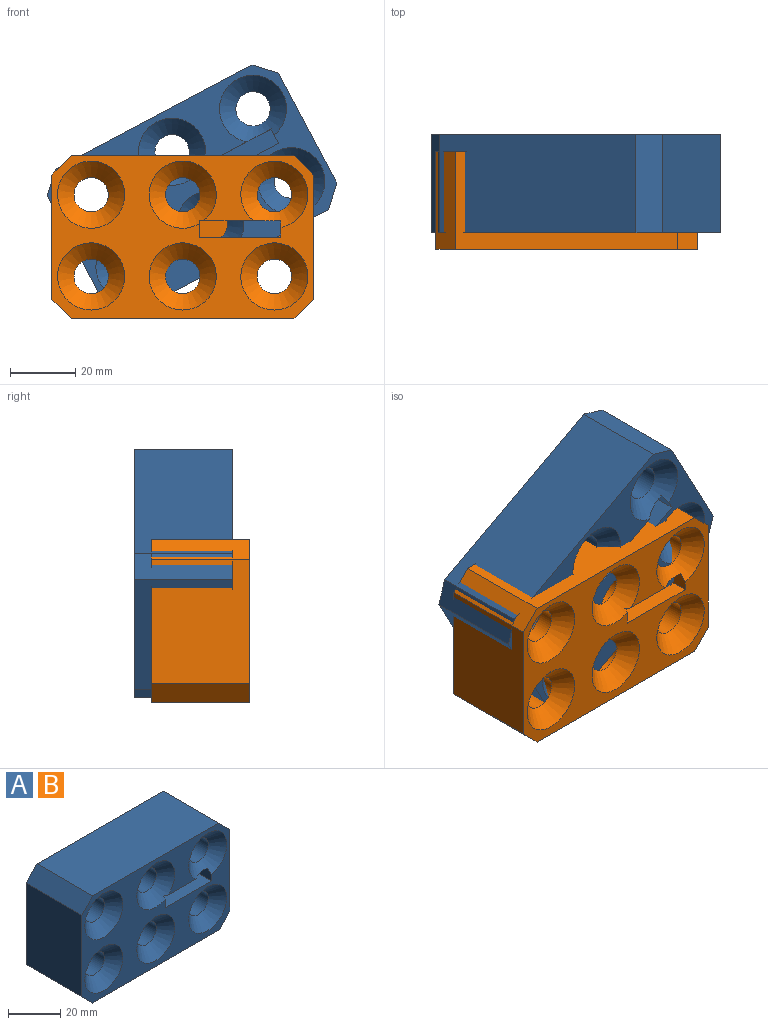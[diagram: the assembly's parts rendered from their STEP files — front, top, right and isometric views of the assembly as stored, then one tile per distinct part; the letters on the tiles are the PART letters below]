
ASSEMBLY  parts=2 mates=1
PART A: 33 faces, bbox 80.2x30.2x50.2 mm
  f0: plane 80x50mm, normal (0,-1,0), area 1837.5mm2, adj f1,f2,f3,f4,f5,f6,f14,f15
  f1: cone r=5.25mm half-angle=45deg, axis (0,-1,0), area 324.3mm2, adj f0,f13,f28,f31
  f2: cone r=5.25mm half-angle=45deg, axis (0,-1,0), area 343.4mm2, adj f0,f11,f28,f29
  f3: plane 68x30mm, normal (0,0,1), area 2040mm2, adj f0,f7,f15,f17
  f4: plane 38x30mm, normal (-1,0,0), area 1140mm2, adj f0,f7,f16,f17
  f5: plane 68x30mm, normal (0,0,-1), area 2040mm2, adj f0,f7,f14,f16
  f6: plane 38x30mm, normal (1,0,0), area 1140mm2, adj f0,f7,f14,f15
  f7: plane 80x50mm, normal (0,1,0), area 1947.6mm2, adj f3,f4,f5,f6,f14,f15,f16,f17
  f8: cylinder r=5.25mm len=20mm, axis (0,-1,0), area 659.7mm2, adj f21,f25
  f9: cylinder r=5.25mm len=20mm, axis (0,-1,0), area 659.7mm2, adj f20,f22
  f10: cylinder r=5.25mm len=20mm, axis (0,-1,0), area 659.7mm2, adj f18,f24
  f11: cylinder r=5.25mm len=20mm, axis (0,-1,0), area 659.7mm2, adj f2,f26
  f12: cylinder r=5.25mm len=20mm, axis (0,-1,0), area 659.7mm2, adj f19,f23
  f13: cylinder r=5.25mm len=20mm, axis (0,-1,0), area 659.7mm2, adj f1,f27
  f14: plane 30x6mm, normal (0.71,0,-0.71), area 254.6mm2, adj f0,f5,f6,f7
  f15: plane 30x6mm, normal (0.71,0,0.71), area 254.6mm2, adj f0,f3,f6,f7
  f16: plane 30x6mm, normal (-0.71,0,-0.71), area 254.6mm2, adj f0,f4,f5,f7
  f17: plane 30x6mm, normal (-0.71,0,0.71), area 254.6mm2, adj f0,f3,f4,f7
  f18: cone r=5.25mm half-angle=45deg, axis (0,-1,0), area 344.3mm2, adj f0,f10
  f19: cone r=5.25mm half-angle=45deg, axis (0,-1,0), area 344.3mm2, adj f0,f12
  f20: cone r=5.25mm half-angle=45deg, axis (0,-1,0), area 344.3mm2, adj f0,f9
  f21: cone r=5.25mm half-angle=45deg, axis (0,-1,0), area 344.3mm2, adj f0,f8
  f22: cone r=5.25mm half-angle=45deg, axis (0,1,0), area 344.3mm2, adj f7,f9
  f23: cone r=5.25mm half-angle=45deg, axis (0,1,0), area 344.3mm2, adj f7,f12
  f24: cone r=5.25mm half-angle=45deg, axis (0,1,0), area 344.3mm2, adj f7,f10
  f25: cone r=5.25mm half-angle=45deg, axis (0,1,0), area 344.3mm2, adj f7,f8
  f26: cone r=5.25mm half-angle=45deg, axis (0,1,0), area 344.3mm2, adj f7,f11
  f27: cone r=5.25mm half-angle=45deg, axis (0,1,0), area 344.3mm2, adj f7,f13
  f28: plane 25.18x25.18mm, normal (0,0,-1), area 610.7mm2, adj f0,f1,f2,f29,f31,f32
  f29: plane 25.02x5.02mm, normal (1,0,0), area 124.6mm2, adj f0,f2,f28,f30,f32
  f30: plane 25x25mm, normal (0,0,1), area 625mm2, adj f0,f29,f31,f32
  f31: plane 25.05x5.05mm, normal (-1,0,0), area 122.9mm2, adj f0,f1,f28,f30,f32
  f32: plane 25x5mm, normal (0,-1,0), area 125mm2, adj f28,f29,f30,f31
PART B: same geometry as A
PLACE A rot(axis=(0,-1,0),27.9deg) t=(9.44,-41.97,0.79)mm
PLACE B t=(-9.75,-46.97,1.99)mm fixed
MATE revolute B.f8 <-> A.f8  axis (0,-1,0) through (2.25,-56.97,39.99)mm
